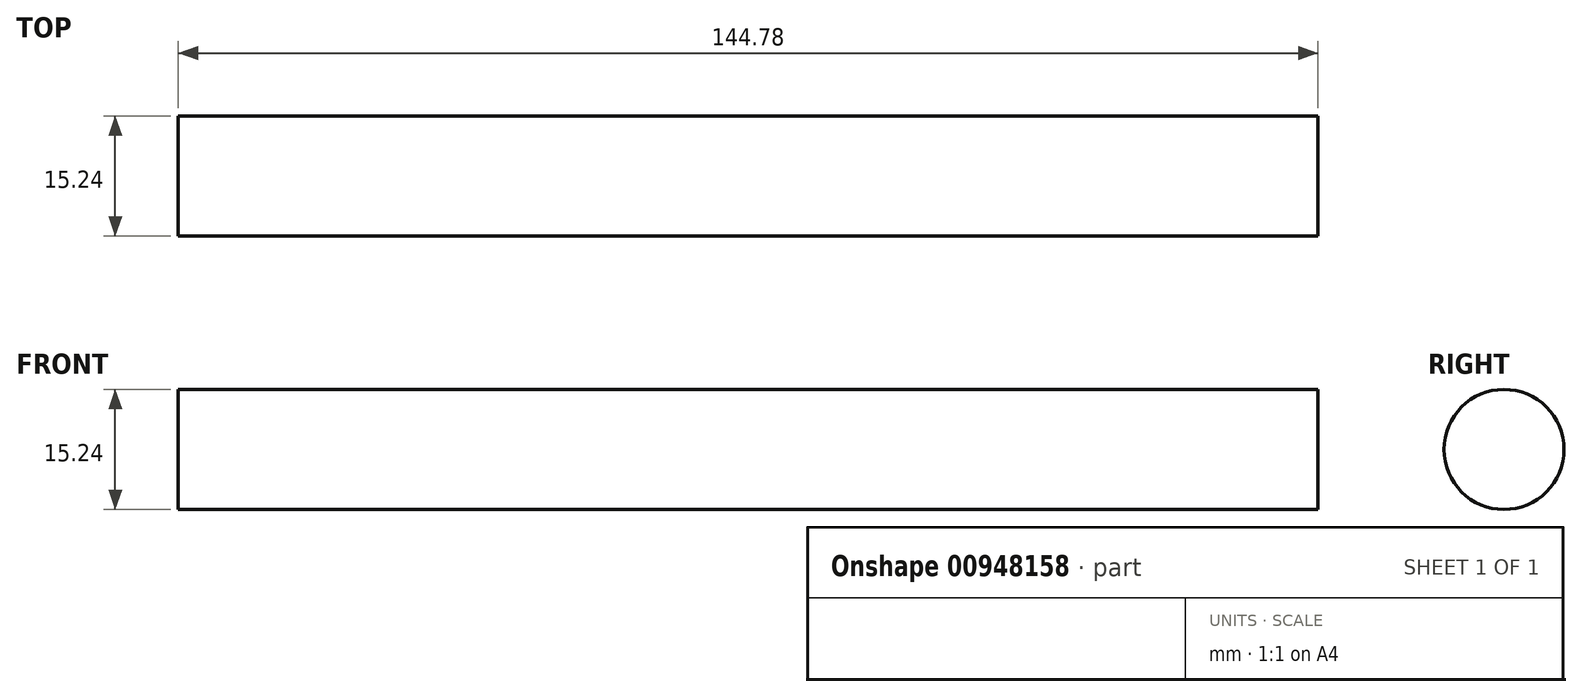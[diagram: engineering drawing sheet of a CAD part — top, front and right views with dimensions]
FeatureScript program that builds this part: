
annotation { "Feature Type Name" : "Feature", "Feature Type Description" : "" }
export const myFeature = defineFeature(function(context is Context, id is Id, definition is map)
    precondition{}
    {
        {
            var Q0;
            Q0=qCreatedBy(makeId("Right.planeOp"),FACE);
            var sketch = newSketch(context, id + "F0", { "sketchPlane" : qUnion([Q0])});
            skCircle(sketch, "E0", {"center": v(-37.4, 26.84) * mm, "radius": 7.62 * mm});
            skSolve(sketch);
        }
        {
            var Q0;
            Q0=makeQuery(id+"F0.imprint","IMPRINT",FACE,{"disambiguationData":[TD([[makeQuery(id+"F0.imprint","IMPRINT",EDGE,{"derivedFrom":sQuery(id+"F0.wireOp",EDGE,"E0")}),1.0]])]});
            extrude(context, id + "F1", {"entities" : qUnion([Q0]), "depth" : 144.78 * mm, "offsetDistance" : 25.4 * mm});
        }
    });
